# Revit family: K施_窓_01_RC開口_抱有_水切有
name_source: partatom
category: 窓
units: mm (PartAtom-declared; Revit-internal decimal feet)

## family parameters
OmniClass タイトル = Windows
OmniClass 番号 = 23.30.20.00
ホスト = 壁
ロード時にボイドで切り取り = はい
共有 = いいえ
常に垂直 = はい
部屋計算ポイント = いいえ

## types (8) — shared parameters
AW見付_H（室内額縁） = 15  [stored 0.0492126 ft]
AW見付_W = 15  [stored 0.0492126 ft]
AW見込 = 70  [stored 0.229659 ft]
RC_下端転び = 20  [stored 0.0656168 ft]
RC_抱き見込 = 85  [stored 0.278871 ft]
RC_抱き転び = 10  [stored 0.0328084 ft]
マテリアル_カイダー床見切り = 施06_木材2_額縁_ﾅﾁｭﾗﾙ
マテリアル_外壁仕上 = 施03_ﾀｲﾙ_045x95_5目地_肌
出入表記（マタギ） = いいえ
幅 = 975  [stored 3.19882 ft]
抱きタイル厚 = 15  [stored 0.0492126 ft]
水切り = はい
解析用性能 = <なし>
開口処理 = ホスト別

## per-type parameters (varying)
| type | RC_H_抱き深さ | RC_H_逃げ_上端 | RC_H_逃げ_下端 | RC_W_抱き深さ | RC_W_逃げ | RC_開口H | RC_開口W | マテリアル_額縁 | 出入表記（掃出し） | 外装抱き仕上 | 掃き出し_見切り（KB.YMバリアフリー） | 水切り働き寸法 | 水切欠込H | 説明 | 額縁_下枠 | 額縁ちり | 額縁見付 | 額縁（上下）負け | 高さ |
| AW-0_腰窓（額有・外壁タイル） | 25  [stored 0.082021 ft] | 35  [stored 0.114829 ft] | 85  [stored 0.278871 ft] | 25  [stored 0.082021 ft] | 30  [stored 0.0984252 ft] | 1200 | 1035 | 施06_木材2_額縁_ﾅﾁｭﾗﾙ | いいえ | はい | いいえ | 125  [stored 0.410105 ft] | 50  [stored 0.164042 ft] | 株式会社和建築設計事務所 | はい | 10  [stored 0.0328084 ft] | 25  [stored 0.082021 ft] | 3  [stored 0.00984252 ft] | 1080  [stored 3.54331 ft] |
| AW-0_掃き出し（額無・外壁タイル） | 25  [stored 0.082021 ft] | 35  [stored 0.114829 ft] | 150 | 25  [stored 0.082021 ft] | 30  [stored 0.0984252 ft] | 2065  [stored 6.77493 ft] | 1035 | 施04_乾式壁_石膏ﾎﾞｰﾄﾞ | はい | はい | はい | 125  [stored 0.410105 ft] | 115  [stored 0.377297 ft] | 株式会社和建築設計事務所 | いいえ | 0  [stored 0 ft] | 12.5  [stored 0.0410105 ft] | 0  [stored 0 ft] | 1880  [stored 6.16798 ft] |
| AW-0_腰窓（額無・外壁タイル） | 25  [stored 0.082021 ft] | 35  [stored 0.114829 ft] | 85  [stored 0.278871 ft] | 25  [stored 0.082021 ft] | 30  [stored 0.0984252 ft] | 1200 | 1035 | 施04_乾式壁_石膏ﾎﾞｰﾄﾞ | いいえ | はい | いいえ | 125  [stored 0.410105 ft] | 50  [stored 0.164042 ft] | 株式会社和建築設計事務所 | はい | 0  [stored 0 ft] | 12.5  [stored 0.0410105 ft] | 0  [stored 0 ft] | 1080  [stored 3.54331 ft] |
| AW-0_掃き出し（額有・外壁タイル） | 25  [stored 0.082021 ft] | 35  [stored 0.114829 ft] | 150 | 25  [stored 0.082021 ft] | 30  [stored 0.0984252 ft] | 2065  [stored 6.77493 ft] | 1035 | 施06_木材2_額縁_ﾅﾁｭﾗﾙ | はい | はい | はい | 125  [stored 0.410105 ft] | 115  [stored 0.377297 ft] | 株式会社和建築設計事務所 | いいえ | 10  [stored 0.0328084 ft] | 25  [stored 0.082021 ft] | 3  [stored 0.00984252 ft] | 1880  [stored 6.16798 ft] |
| AW-0_腰壁（額無・外壁吹付） | 40  [stored 0.131234 ft] | 20  [stored 0.0656168 ft] | 85  [stored 0.278871 ft] | 40  [stored 0.131234 ft] | 15  [stored 0.0492126 ft] | 1185 | 1005  [stored 3.29724 ft] | 施04_乾式壁_石膏ﾎﾞｰﾄﾞ | いいえ | いいえ | いいえ | 115  [stored 0.377297 ft] | 50  [stored 0.164042 ft] |  | はい | 0  [stored 0 ft] | 12.5  [stored 0.0410105 ft] | 0  [stored 0 ft] | 1080  [stored 3.54331 ft] |
| AW-0_掃き出し（額無・外壁吹付） | 40  [stored 0.131234 ft] | 20  [stored 0.0656168 ft] | 150 | 40  [stored 0.131234 ft] | 15  [stored 0.0492126 ft] | 2050  [stored 6.72572 ft] | 1005  [stored 3.29724 ft] | 施04_乾式壁_石膏ﾎﾞｰﾄﾞ | はい | いいえ | はい | 115  [stored 0.377297 ft] | 115  [stored 0.377297 ft] | 株式会社和建築設計事務所 | いいえ | 0  [stored 0 ft] | 12.5  [stored 0.0410105 ft] | 0  [stored 0 ft] | 1880  [stored 6.16798 ft] |
| AW-0_腰壁（額有・外壁吹付） | 40  [stored 0.131234 ft] | 20  [stored 0.0656168 ft] | 85  [stored 0.278871 ft] | 40  [stored 0.131234 ft] | 15  [stored 0.0492126 ft] | 1185 | 1005  [stored 3.29724 ft] | 施06_木材2_額縁_ﾅﾁｭﾗﾙ | いいえ | いいえ | いいえ | 115  [stored 0.377297 ft] | 50  [stored 0.164042 ft] | 株式会社和建築設計事務所 | はい | 10  [stored 0.0328084 ft] | 25  [stored 0.082021 ft] | 3  [stored 0.00984252 ft] | 1080  [stored 3.54331 ft] |
| AW-0_掃き出し（額有・外壁吹付） | 40  [stored 0.131234 ft] | 20  [stored 0.0656168 ft] | 150 | 40  [stored 0.131234 ft] | 15  [stored 0.0492126 ft] | 2050  [stored 6.72572 ft] | 1005  [stored 3.29724 ft] | 施06_木材2_額縁_ﾅﾁｭﾗﾙ | はい | いいえ | はい | 115  [stored 0.377297 ft] | 115  [stored 0.377297 ft] | 株式会社和建築設計事務所 | いいえ | 10  [stored 0.0328084 ft] | 25  [stored 0.082021 ft] | 3  [stored 0.00984252 ft] | 1880  [stored 6.16798 ft] |

note: [stored X ft] marks values corroborated as IEEE doubles in the binary element streams (Revit-internal decimal feet)
